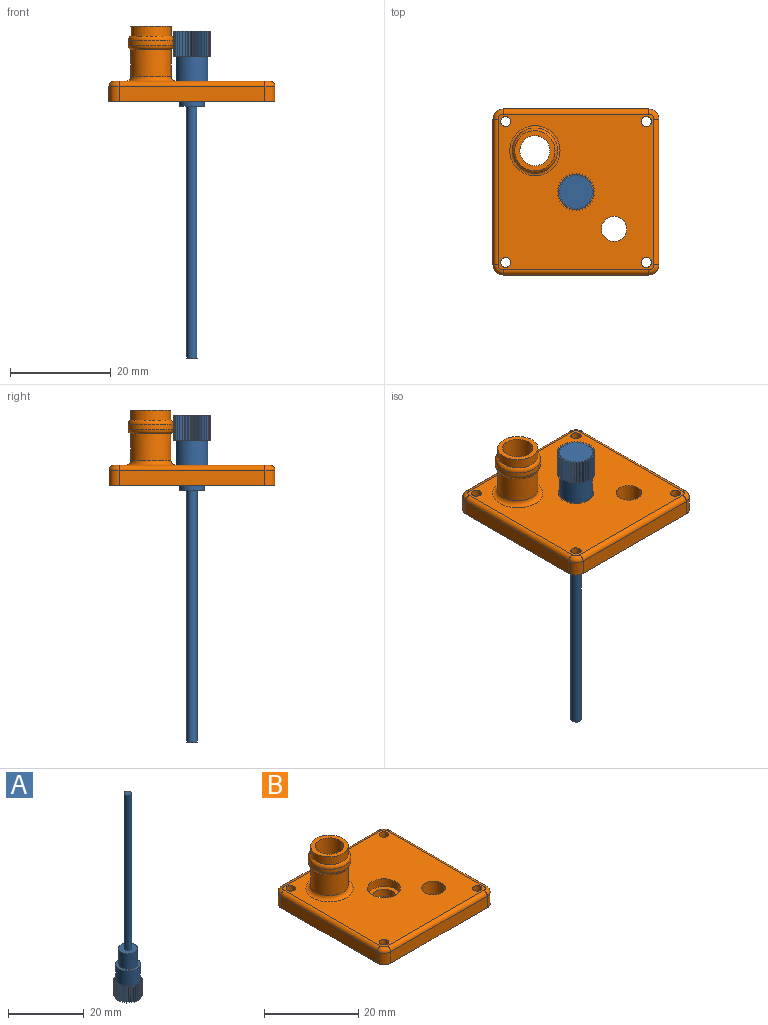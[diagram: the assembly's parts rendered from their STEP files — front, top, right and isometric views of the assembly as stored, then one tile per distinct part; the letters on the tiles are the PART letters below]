
ASSEMBLY  parts=2 mates=1
PART A: 117 faces, bbox 7.5x7.5x65 mm
  f0: cylinder r=3.25mm len=6.5mm, axis (0,0,-1), area 102.1mm2, adj f5,f9,f12,f15,f18,f21,f24,f27
  f1: cylinder r=1mm len=50mm, axis (0,0,-1), area 314.2mm2, adj f2,f4
  f2: plane 2x2mm, normal (0,0,1), area 3.1mm2, adj f1
  f3: cylinder r=2.5mm len=5mm, axis (0,0,-1), area 78.5mm2, adj f4,f5
  f4: plane 5x5mm, normal (0,0,1), area 16.5mm2, adj f1,f3
  f5: plane 6.5x6.5mm, normal (0,0,1), area 13.5mm2, adj f0,f3
  f6: plane 7.5x7.5mm, normal (0,0,-1), area 38.2mm2, adj f7,f8,f10,f11,f13,f14,f16,f17
  f7: plane 5x0.45mm, normal (0.68,-0.73,0), area 3.1mm2, adj f6,f8,f9,f114
  f8: plane 5x0.57mm, normal (0.38,0.92,0), area 3.1mm2, adj f6,f7,f9,f10
  f9: plane 0.66x0.57mm, normal (0,0,1), area 0.2mm2, adj f0,f7,f8
  f10: plane 5x0.4mm, normal (0.71,-0.7,0), area 2.8mm2, adj f6,f8,f11,f12
  f11: plane 5x0.59mm, normal (0.2,0.98,0), area 3mm2, adj f6,f10,f12,f13
  f12: plane 0.59x0.52mm, normal (0,0,1), area 0.1mm2, adj f0,f10,f11
  f13: plane 5x0.48mm, normal (0.84,-0.55,0), area 2.9mm2, adj f6,f11,f14,f15
  f14: plane 5x0.58mm, normal (-0.03,1,0), area 2.9mm2, adj f6,f13,f15,f16
  f15: plane 0.58x0.48mm, normal (0,0,1), area 0.1mm2, adj f0,f13,f14
  f16: plane 5x0.55mm, normal (0.93,-0.36,0), area 2.9mm2, adj f6,f14,f17,f18
  f17: plane 5x0.55mm, normal (-0.25,0.97,0), area 2.8mm2, adj f6,f16,f18,f19
  f18: plane 0.55x0.55mm, normal (0,0,1), area 0.1mm2, adj f0,f16,f17
  f19: plane 5x0.6mm, normal (0.99,-0.14,0), area 3mm2, adj f6,f17,f20,f21
  f20: plane 5x0.51mm, normal (-0.42,0.91,0), area 2.8mm2, adj f6,f19,f21,f22
  f21: plane 0.6x0.51mm, normal (0,0,1), area 0.1mm2, adj f0,f19,f20
  f22: plane 5x0.61mm, normal (1,0.03,0), area 3mm2, adj f6,f20,f23,f24
  f23: plane 5x0.47mm, normal (-0.55,0.83,0), area 2.8mm2, adj f6,f22,f24,f25
  f24: plane 0.61x0.49mm, normal (0,0,1), area 0.1mm2, adj f0,f22,f23
  f25: plane 5x0.59mm, normal (0.98,0.19,0), area 3mm2, adj f6,f23,f26,f27
  f26: plane 5x0.42mm, normal (-0.68,0.74,0), area 2.9mm2, adj f6,f25,f27,f29
  f27: plane 0.59x0.54mm, normal (0,0,1), area 0.1mm2, adj f0,f25,f26
  f28: plane 5x0.45mm, normal (-0.77,0.64,0), area 3mm2, adj f6,f29,f30,f31
  f29: plane 5x0.56mm, normal (0.94,0.34,0), area 3mm2, adj f6,f26,f28,f30
  f30: plane 0.59x0.56mm, normal (0,0,1), area 0.1mm2, adj f0,f28,f29
  f31: plane 5x0.51mm, normal (0.89,0.46,0), area 2.9mm2, adj f6,f28,f32,f33
  f32: plane 5x0.51mm, normal (-0.89,0.46,0), area 2.9mm2, adj f6,f31,f33,f34
  f33: plane 0.53x0.51mm, normal (0,0,1), area 0.1mm2, adj f0,f31,f32
  f34: plane 5x0.45mm, normal (0.77,0.64,0), area 3mm2, adj f6,f32,f35,f36
  f35: plane 5x0.56mm, normal (-0.94,0.34,0), area 3mm2, adj f6,f34,f36,f37
  f36: plane 0.59x0.56mm, normal (0,0,1), area 0.1mm2, adj f0,f34,f35
  f37: plane 5x0.42mm, normal (0.68,0.74,0), area 2.9mm2, adj f6,f35,f38,f39
  f38: plane 5x0.59mm, normal (-0.98,0.19,0), area 3mm2, adj f6,f37,f39,f40
  f39: plane 0.59x0.54mm, normal (0,0,1), area 0.1mm2, adj f0,f37,f38
  f40: plane 5x0.47mm, normal (0.55,0.83,0), area 2.8mm2, adj f6,f38,f41,f42
  f41: plane 5x0.61mm, normal (-1,0.03,0), area 3mm2, adj f6,f40,f42,f43
  f42: plane 0.61x0.49mm, normal (0,0,1), area 0.1mm2, adj f0,f40,f41
  f43: plane 5x0.51mm, normal (0.42,0.91,0), area 2.8mm2, adj f6,f41,f44,f45
  f44: plane 5x0.6mm, normal (-0.99,-0.14,0), area 3mm2, adj f6,f43,f45,f46
  f45: plane 0.6x0.51mm, normal (0,0,1), area 0.1mm2, adj f0,f43,f44
  f46: plane 5x0.55mm, normal (0.25,0.97,0), area 2.8mm2, adj f6,f44,f47,f48
  f47: plane 5x0.55mm, normal (-0.93,-0.36,0), area 2.9mm2, adj f6,f46,f48,f49
  f48: plane 0.55x0.55mm, normal (0,0,1), area 0.1mm2, adj f0,f46,f47
  f49: plane 5x0.58mm, normal (0.03,1,0), area 2.9mm2, adj f6,f47,f50,f51
  f50: plane 5x0.48mm, normal (-0.84,-0.55,0), area 2.9mm2, adj f6,f49,f51,f52
  f51: plane 0.58x0.48mm, normal (0,0,1), area 0.1mm2, adj f0,f49,f50
  f52: plane 5x0.59mm, normal (-0.2,0.98,0), area 3mm2, adj f6,f50,f53,f54
  f53: plane 5x0.4mm, normal (-0.71,-0.7,0), area 2.8mm2, adj f6,f52,f54,f56
  f54: plane 0.59x0.52mm, normal (0,0,1), area 0.1mm2, adj f0,f52,f53
  f55: plane 5x0.45mm, normal (-0.68,-0.73,0), area 3.1mm2, adj f6,f56,f57,f58
  f56: plane 5x0.57mm, normal (-0.38,0.92,0), area 3.1mm2, adj f6,f53,f55,f57
  f57: plane 0.66x0.57mm, normal (0,0,1), area 0.2mm2, adj f0,f55,f56
  f58: plane 5x0.51mm, normal (-0.42,0.91,0), area 2.8mm2, adj f6,f55,f59,f61
  f59: plane 5x0.01mm, normal (-1,0,0), area 0mm2, adj f6,f58,f60,f61
  f60: plane 5x0.51mm, normal (-0.42,-0.91,0), area 2.8mm2, adj f6,f59,f61,f62
  f61: plane 0.51x0.48mm, normal (0,0,1), area 0.1mm2, adj f0,f58,f59,f60
  f62: plane 5x0.45mm, normal (-0.68,0.73,0), area 3.1mm2, adj f6,f60,f63,f64
  f63: plane 5x0.57mm, normal (-0.38,-0.92,0), area 3.1mm2, adj f6,f62,f64,f65
  f64: plane 0.66x0.57mm, normal (0,0,1), area 0.2mm2, adj f0,f62,f63
  f65: plane 5x0.4mm, normal (-0.71,0.7,0), area 2.8mm2, adj f6,f63,f66,f67
  f66: plane 5x0.59mm, normal (-0.2,-0.98,0), area 3mm2, adj f6,f65,f67,f68
  f67: plane 0.59x0.52mm, normal (0,0,1), area 0.1mm2, adj f0,f65,f66
  f68: plane 5x0.48mm, normal (-0.84,0.55,0), area 2.9mm2, adj f6,f66,f69,f70
  f69: plane 5x0.58mm, normal (0.03,-1,0), area 2.9mm2, adj f6,f68,f70,f71
  f70: plane 0.58x0.48mm, normal (0,0,1), area 0.1mm2, adj f0,f68,f69
  f71: plane 5x0.55mm, normal (-0.93,0.36,0), area 2.9mm2, adj f6,f69,f72,f73
  f72: plane 5x0.55mm, normal (0.25,-0.97,0), area 2.8mm2, adj f6,f71,f73,f74
  f73: plane 0.55x0.55mm, normal (0,0,1), area 0.1mm2, adj f0,f71,f72
  f74: plane 5x0.6mm, normal (-0.99,0.14,0), area 3mm2, adj f6,f72,f75,f76
  f75: plane 5x0.51mm, normal (0.42,-0.91,0), area 2.8mm2, adj f6,f74,f76,f77
  f76: plane 0.6x0.51mm, normal (0,0,1), area 0.1mm2, adj f0,f74,f75
  f77: plane 5x0.61mm, normal (-1,-0.03,0), area 3mm2, adj f6,f75,f78,f79
  f78: plane 5x0.47mm, normal (0.55,-0.83,0), area 2.8mm2, adj f6,f77,f79,f80
  f79: plane 0.61x0.49mm, normal (0,0,1), area 0.1mm2, adj f0,f77,f78
  f80: plane 5x0.59mm, normal (-0.98,-0.19,0), area 3mm2, adj f6,f78,f81,f82
  f81: plane 5x0.42mm, normal (0.68,-0.74,0), area 2.9mm2, adj f6,f80,f82,f83
  f82: plane 0.59x0.54mm, normal (0,0,1), area 0.1mm2, adj f0,f80,f81
  f83: plane 5x0.56mm, normal (-0.94,-0.34,0), area 3mm2, adj f6,f81,f84,f85
  f84: plane 5x0.45mm, normal (0.77,-0.64,0), area 3mm2, adj f6,f83,f85,f86
  f85: plane 0.59x0.56mm, normal (0,0,1), area 0.1mm2, adj f0,f83,f84
  f86: plane 5x0.51mm, normal (-0.89,-0.46,0), area 2.9mm2, adj f6,f84,f87,f88
  f87: plane 5x0.51mm, normal (0.89,-0.46,0), area 2.9mm2, adj f6,f86,f88,f89
  f88: plane 0.53x0.51mm, normal (0,0,1), area 0.1mm2, adj f0,f86,f87
  f89: plane 5x0.45mm, normal (-0.77,-0.64,0), area 3mm2, adj f6,f87,f90,f91
  f90: plane 5x0.56mm, normal (0.94,-0.34,0), area 3mm2, adj f6,f89,f91,f92
  f91: plane 0.59x0.56mm, normal (0,0,1), area 0.1mm2, adj f0,f89,f90
  f92: plane 5x0.42mm, normal (-0.68,-0.74,0), area 2.9mm2, adj f6,f90,f93,f94
  f93: plane 5x0.59mm, normal (0.98,-0.19,0), area 3mm2, adj f6,f92,f94,f95
  f94: plane 0.59x0.54mm, normal (0,0,1), area 0.1mm2, adj f0,f92,f93
  f95: plane 5x0.47mm, normal (-0.55,-0.83,0), area 2.8mm2, adj f6,f93,f96,f97
  f96: plane 5x0.61mm, normal (1,-0.03,0), area 3mm2, adj f6,f95,f97,f98
  f97: plane 0.61x0.49mm, normal (0,0,1), area 0.1mm2, adj f0,f95,f96
  f98: plane 5x0.51mm, normal (-0.42,-0.91,0), area 2.8mm2, adj f6,f96,f99,f100
  f99: plane 5x0.6mm, normal (0.99,0.14,0), area 3mm2, adj f6,f98,f100,f101
  f100: plane 0.6x0.51mm, normal (0,0,1), area 0.1mm2, adj f0,f98,f99
  f101: plane 5x0.55mm, normal (-0.25,-0.97,0), area 2.8mm2, adj f6,f99,f102,f103
  f102: plane 5x0.55mm, normal (0.93,0.36,0), area 2.9mm2, adj f6,f101,f103,f104
  f103: plane 0.55x0.55mm, normal (0,0,1), area 0.1mm2, adj f0,f101,f102
  f104: plane 5x0.58mm, normal (-0.03,-1,0), area 2.9mm2, adj f6,f102,f105,f106
  f105: plane 5x0.48mm, normal (0.84,0.55,0), area 2.9mm2, adj f6,f104,f106,f107
  f106: plane 0.58x0.48mm, normal (0,0,1), area 0.1mm2, adj f0,f104,f105
  f107: plane 5x0.59mm, normal (0.2,-0.98,0), area 3mm2, adj f6,f105,f108,f109
  f108: plane 5x0.4mm, normal (0.71,0.7,0), area 2.8mm2, adj f6,f107,f109,f110
  f109: plane 0.59x0.52mm, normal (0,0,1), area 0.1mm2, adj f0,f107,f108
  f110: plane 5x0.57mm, normal (0.38,-0.92,0), area 3.1mm2, adj f6,f108,f111,f112
  f111: plane 5x0.45mm, normal (0.68,0.73,0), area 3.1mm2, adj f6,f110,f112,f115
  f112: plane 0.66x0.57mm, normal (0,0,1), area 0.2mm2, adj f0,f110,f111
  f113: plane 5x0.01mm, normal (1,0,0), area 0mm2, adj f6,f114,f115,f116
  f114: plane 5x0.51mm, normal (0.42,0.91,0), area 2.8mm2, adj f6,f7,f113,f116
  f115: plane 5x0.51mm, normal (0.42,-0.91,0), area 2.8mm2, adj f6,f111,f113,f116
  f116: plane 0.51x0.48mm, normal (0,0,1), area 0.1mm2, adj f0,f113,f114,f115
PART B: 34 faces, bbox 33.3x33.3x15 mm
  f0: plane 31x31mm, normal (0,0,1), area 810.9mm2, adj f5,f6,f8,f9,f10,f11,f19,f20
  f1: cylinder r=4mm len=8mm, axis (0,0,-1), area 133.2mm2, adj f17,f33
  f2: plane 29x3mm, normal (1,0,0), area 87mm2, adj f12,f20,f23,f29
  f3: plane 29x3mm, normal (0,1,0), area 87mm2, adj f12,f19,f27,f29
  f4: plane 29x3mm, normal (-1,0,0), area 87mm2, adj f12,f21,f25,f27
  f5: cylinder r=2.5mm len=5mm, axis (0,0,-1), area 62.8mm2, adj f0,f12
  f6: cylinder r=1mm len=4mm, axis (0,0,-1), area 25.1mm2, adj f0,f12
  f7: plane 29x3mm, normal (0,-1,0), area 87mm2, adj f12,f22,f23,f25
  f8: cylinder r=1mm len=4mm, axis (0,0,-1), area 25.1mm2, adj f0,f12
  f9: cylinder r=1mm len=4mm, axis (0,0,-1), area 25.1mm2, adj f0,f12
  f10: cylinder r=1mm len=4mm, axis (0,0,-1), area 25.1mm2, adj f0,f12
  f11: cylinder r=3.5mm len=7mm, axis (0,0,-1), area 44mm2, adj f0,f32
  f12: plane 33x33mm, normal (0,0,-1), area 1005.5mm2, adj f2,f3,f4,f5,f6,f7,f8,f9
  f13: cylinder r=3mm len=15mm, axis (0,0,-1), area 282.7mm2, adj f12,f15
  f14: cylinder r=4mm len=8mm, axis (0,0,-1), area 50.3mm2, adj f15,f18
  f15: plane 8x8mm, normal (0,0,1), area 22mm2, adj f13,f14
  f16: cylinder r=4.5mm len=9mm, axis (0,0,-1), area 27.4mm2, adj f17,f18
  f17: torus R=3.5mm, axis (0,0,-1), area 28.5mm2, adj f1,f16
  f18: torus R=3.5mm, axis (0,0,1), area 28.5mm2, adj f14,f16
  f19: cylinder r=1mm len=29mm, axis (1,0,0), area 45.6mm2, adj f0,f3,f28,f30
  f20: cylinder r=1mm len=29mm, axis (0,-1,0), area 45.6mm2, adj f0,f2,f24,f30
  f21: cylinder r=1mm len=29mm, axis (0,1,0), area 45.6mm2, adj f0,f4,f26,f28
  f22: cylinder r=1mm len=29mm, axis (-1,0,0), area 45.6mm2, adj f0,f7,f24,f26
  f23: cylinder r=2mm len=3mm, axis (0,0,-1), area 9.4mm2, adj f2,f7,f12,f24
  f24: torus R=1mm, axis (0,0,1), area 4mm2, adj f0,f20,f22,f23
  f25: cylinder r=2mm len=3mm, axis (0,0,1), area 9.4mm2, adj f4,f7,f12,f26
  f26: torus R=1mm, axis (0,0,1), area 4mm2, adj f0,f21,f22,f25
  f27: cylinder r=2mm len=3mm, axis (0,0,-1), area 9.4mm2, adj f3,f4,f12,f28
  f28: torus R=1mm, axis (0,0,1), area 4mm2, adj f0,f19,f21,f27
  f29: cylinder r=2mm len=3mm, axis (0,0,1), area 9.4mm2, adj f2,f3,f12,f30
  f30: torus R=1mm, axis (0,0,1), area 4mm2, adj f0,f19,f20,f29
  f31: cylinder r=2.5mm len=5mm, axis (0,0,-1), area 31.4mm2, adj f12,f32
  f32: plane 7x7mm, normal (0,0,1), area 18.8mm2, adj f11,f31
  f33: torus R=5mm, axis (0,0,1), area 43.1mm2, adj f0,f1
PLACE A rot(axis=(0,1,0),180deg) t=(32.92,24.13,3.05)mm
PLACE B t=(32.92,24.13,-10.95)mm
MATE slider B.f11 <-> A.f0  axis (0,0,1) through (32.92,24.13,-6.95)mm
